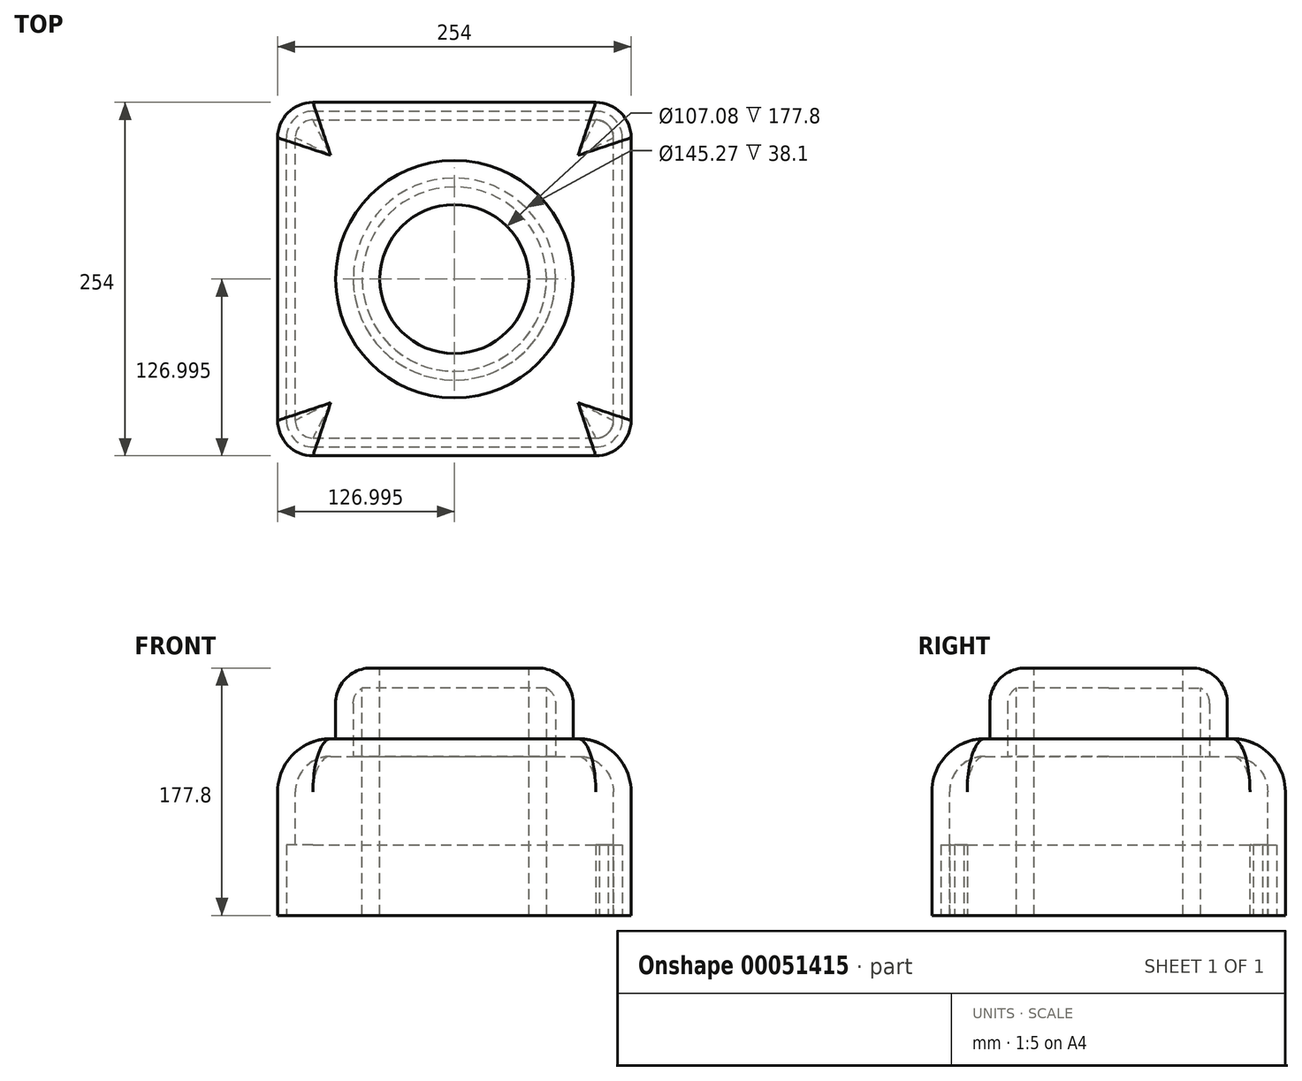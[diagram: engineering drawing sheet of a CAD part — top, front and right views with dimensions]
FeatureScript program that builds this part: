
annotation { "Feature Type Name" : "Feature", "Feature Type Description" : "" }
export const myFeature = defineFeature(function(context is Context, id is Id, definition is map)
    precondition{}
    {
        {
            var Q0;
            Q0=qCreatedBy(makeId("Top.planeOp"),FACE);
            var sketch = newSketch(context, id + "F0", { "sketchPlane" : qUnion([Q0])});
            skLineSegment(sketch, "E0.bottom", {"start": v(-164.41, -127.92) * mm, "end": v(89.59, -127.92) * mm});
            skLineSegment(sketch, "E0.top", {"start": v(-164.41, 126.08) * mm, "end": v(89.59, 126.08) * mm});
            skLineSegment(sketch, "E0.left", {"start": v(-164.41, -127.92) * mm, "end": v(-164.41, 126.08) * mm});
            skLineSegment(sketch, "E0.right", {"start": v(89.59, -127.92) * mm, "end": v(89.59, 126.08) * mm});
            skSolve(sketch);
        }
        {
            var Q0;
            Q0 = qSketchRegion(id + "F0", true);
            extrude(context, id + "F1", {"entities" : qUnion([Q0]), "depth" : 127 * mm});
        }
        {
            var Q0;
            Q0=makeQuery(id+"F1.opExtrude","CAP_FACE",FACE,{"disambiguationData":[OSD([sQuery(id+"F0.wireOp",EDGE,"E0.bottom"),sQuery(id+"F0.wireOp",EDGE,"E0.top"),sQuery(id+"F0.wireOp",EDGE,"E0.left"),sQuery(id+"F0.wireOp",EDGE,"E0.right")])],"isStart":false});
            var sketch = newSketch(context, id + "F2", { "sketchPlane" : qUnion([Q0])});
            skLineSegment(sketch, "E1", {"start": v(-164.41, 126.08) * mm, "end": v(-164.41, -127.92) * mm});
            skPoint(sketch, "E2.second.point", {"position": v(89.59, -127.92) * mm});
            skPoint(sketch, "E2.third.point", {"position": v(89.59, 126.08) * mm});
            skCircle(sketch, "E3", {"center": v(-37.41, -0.92) * mm, "radius": 85.34 * mm});
            skSolve(sketch);
        }
        {
            var Q0;
            Q0 = qSketchRegion(id + "F2", true);
            extrude(context, id + "F3", {"entities" : qUnion([Q0]), "operationType" : NewBodyOperationType.ADD, "depth" : 50.8 * mm});
        }
        {
            var Q0;
            Q0=makeQuery(id+"F3.opExtrude","CAP_FACE",FACE,{"disambiguationData":[OSD([sQuery(id+"F2.wireOp",EDGE,"E3")])],"isStart":false});
            var sketch = newSketch(context, id + "F4", { "sketchPlane" : qUnion([Q0])});
            skCircle(sketch, "E4", {"center": v(-37.41, -0.92) * mm, "radius": 53.54 * mm});
            skSolve(sketch);
        }
        {
            var Q0;
            Q0=makeQuery(id+"F4.imprint","IMPRINT",FACE,{"disambiguationData":[TD([[makeQuery(id+"F4.imprint","IMPRINT",EDGE,{"derivedFrom":sQuery(id+"F4.wireOp",EDGE,"E4")}),1.0]])]});
            var Q1;
            Q1=sQuery(id+"F4.wireOp",EDGE,"E4");
            var Q2;
            Q2=makeQuery(id+"F1.opExtrude","CAP_FACE",FACE,{"disambiguationData":[OSD([sQuery(id+"F0.wireOp",EDGE,"E0.bottom"),sQuery(id+"F0.wireOp",EDGE,"E0.top"),sQuery(id+"F0.wireOp",EDGE,"E0.left"),sQuery(id+"F0.wireOp",EDGE,"E0.right")])],"isStart":true});
            extrude(context, id + "F5", {"entities" : qUnion([Q0]), "operationType" : NewBodyOperationType.REMOVE, "surfaceEntities" : qUnion([Q1]), "endBound" : BoundingType.UP_TO_SURFACE, "oppositeDirection" : true, "endBoundEntityFace" : qUnion([Q2]), "depth" : 25.4 * mm});
        }
        {
            var Q0;
            Q0=makeQuery(id+"F1.opExtrude","SWEPT_EDGE",EDGE,{"disambiguationData":[OSD([sQuery(id+"F0.wireOp",EDGE,"E0.bottom"),sQuery(id+"F0.wireOp",EDGE,"E0.left")])]});
            var Q1;
            Q1=makeQuery(id+"F1.opExtrude","SWEPT_EDGE",EDGE,{"disambiguationData":[OSD([sQuery(id+"F0.wireOp",EDGE,"E0.bottom"),sQuery(id+"F0.wireOp",EDGE,"E0.right")])]});
            var Q2;
            Q2=makeQuery(id+"F1.opExtrude","SWEPT_EDGE",EDGE,{"disambiguationData":[OSD([sQuery(id+"F0.wireOp",EDGE,"E0.top"),sQuery(id+"F0.wireOp",EDGE,"E0.left")])]});
            var Q3;
            Q3=makeQuery(id+"F1.opExtrude","SWEPT_EDGE",EDGE,{"disambiguationData":[OSD([sQuery(id+"F0.wireOp",EDGE,"E0.top"),sQuery(id+"F0.wireOp",EDGE,"E0.right")])]});
            fillet(context, id + "F6", {"entities" : qUnion([Q0, Q1, Q2, Q3]), "radius" : 25.4 * mm, "tangentPropagation" : true, "allowEdgeOverflow" : false});
        }
        {
            var Q0;
            Q0=makeQuery(id+"F1.opExtrude","CAP_EDGE",EDGE,{"disambiguationData":[OSD([sQuery(id+"F0.wireOp",EDGE,"E0.top")])],"isStart":false});
            var Q1;
            Q1=makeQuery(id+"F1.opExtrude","CAP_EDGE",EDGE,{"disambiguationData":[OSD([sQuery(id+"F0.wireOp",EDGE,"E0.right")])],"isStart":false});
            var Q2;
            Q2=makeQuery(id+"F1.opExtrude","CAP_EDGE",EDGE,{"disambiguationData":[OSD([sQuery(id+"F0.wireOp",EDGE,"E0.left")])],"isStart":false});
            var Q3;
            Q3=makeQuery(id+"F1.opExtrude","CAP_EDGE",EDGE,{"disambiguationData":[OSD([sQuery(id+"F0.wireOp",EDGE,"E0.bottom")])],"isStart":false});
            fillet(context, id + "F7", {"entities" : qUnion([Q0, Q1, Q2, Q3]), "radius" : 38.1 * mm, "tangentPropagation" : true, "allowEdgeOverflow" : false});
        }
        {
            var Q0;
            Q0=makeQuery(id+"F3.opExtrude","CAP_EDGE",EDGE,{"disambiguationData":[OSD([sQuery(id+"F2.wireOp",EDGE,"E3")])],"isStart":false});
            fillet(context, id + "F8", {"entities" : qUnion([Q0]), "radius" : 25.4 * mm, "tangentPropagation" : true, "allowEdgeOverflow" : false});
        }
        {
            var Q0;
            Q0=makeQuery(id+"F1.opExtrude","CAP_FACE",FACE,{"disambiguationData":[OSD([sQuery(id+"F0.wireOp",EDGE,"E0.bottom"),sQuery(id+"F0.wireOp",EDGE,"E0.top"),sQuery(id+"F0.wireOp",EDGE,"E0.left"),sQuery(id+"F0.wireOp",EDGE,"E0.right")])],"isStart":true});
            shell(context, id + "F9", {"entities" : qUnion([Q0]), "thickness" : 12.7 * mm});
        }
        {
            var Q0;
            Q0=makeQuery(id+"F1.opExtrude","CAP_FACE",FACE,{"disambiguationData":[OSD([sQuery(id+"F0.wireOp",EDGE,"E0.bottom"),sQuery(id+"F0.wireOp",EDGE,"E0.top"),sQuery(id+"F0.wireOp",EDGE,"E0.left"),sQuery(id+"F0.wireOp",EDGE,"E0.right")])],"isStart":true});
            var sketch = newSketch(context, id + "F10", { "sketchPlane" : qUnion([Q0])});
            skArc(sketch, "E5.0", {"start": v(-139.01, 121.57) * mm, "mid": v(-152.49, 116) * mm, "end": v(-158.06, 102.52) * mm});
            skLineSegment(sketch, "E5.1", {"start": v(-139.01, 121.57) * mm, "end": v(64.19, 121.57) * mm});
            skLineSegment(sketch, "E5.2", {"start": v(-158.06, 102.52) * mm, "end": v(-158.06, -100.68) * mm});
            skArc(sketch, "E5.3", {"start": v(83.24, 102.52) * mm, "mid": v(77.66, 116) * mm, "end": v(64.19, 121.57) * mm});
            skArc(sketch, "E5.4", {"start": v(-158.06, -100.68) * mm, "mid": v(-152.49, -114.15) * mm, "end": v(-139.01, -119.73) * mm});
            skLineSegment(sketch, "E5.5", {"start": v(-139.01, -119.73) * mm, "end": v(64.19, -119.73) * mm});
            skArc(sketch, "E5.6", {"start": v(64.19, -119.73) * mm, "mid": v(77.66, -114.15) * mm, "end": v(83.24, -100.68) * mm});
            skLineSegment(sketch, "E5.7", {"start": v(83.24, 102.52) * mm, "end": v(83.24, -100.68) * mm});
            skLineSegment(sketch, "E6.0", {"start": v(-151.71, 102.52) * mm, "end": v(-151.71, -100.68) * mm});
            skArc(sketch, "E7.0", {"start": v(-139.01, 115.22) * mm, "mid": v(-148, 111.5) * mm, "end": v(-151.71, 102.52) * mm});
            skLineSegment(sketch, "E8.0", {"start": v(-139.01, 115.22) * mm, "end": v(64.19, 115.22) * mm});
            skFitSpline(sketch, "E9", {"points": [v(64.19, 115.22) * mm, v(65.02, 115.22) * mm, v(65.84, 115.14) * mm, v(66.66, 114.98) * mm, v(67.48, 114.82) * mm, v(68.27, 114.58) * mm, v(69.05, 114.26) * mm, v(69.82, 113.94) * mm, v(70.55, 113.55) * mm, v(71.24, 113.08) * mm, v(71.93, 112.62) * mm, v(72.58, 112.1) * mm, v(73.17, 111.5) * mm, v(73.75, 110.92) * mm, v(74.28, 110.27) * mm, v(74.74, 109.58) * mm, v(75.2, 108.89) * mm, v(75.6, 108.16) * mm, v(75.92, 107.39) * mm, v(76.24, 106.61) * mm, v(76.48, 105.82) * mm, v(76.64, 105) * mm, v(76.8, 104.18) * mm, v(76.89, 103.36) * mm, v(76.89, 102.52) * mm]});
            skLineSegment(sketch, "E10.0", {"start": v(76.89, 102.52) * mm, "end": v(76.89, -100.68) * mm});
            skFitSpline(sketch, "E11", {"points": [v(76.89, -100.68) * mm, v(76.89, -101.5) * mm, v(76.8, -102.33) * mm, v(76.64, -103.15) * mm, v(76.48, -103.97) * mm, v(76.24, -104.76) * mm, v(75.92, -105.54) * mm, v(75.6, -106.3) * mm, v(75.2, -107.04) * mm, v(74.74, -107.73) * mm, v(74.28, -108.42) * mm, v(73.76, -109.07) * mm, v(73.17, -109.66) * mm, v(72.58, -110.24) * mm, v(71.93, -110.77) * mm, v(71.24, -111.23) * mm, v(70.55, -111.7) * mm, v(69.82, -112.09) * mm, v(69.05, -112.4) * mm, v(68.28, -112.73) * mm, v(67.48, -112.97) * mm, v(66.66, -113.13) * mm, v(65.85, -113.3) * mm, v(65.02, -113.38) * mm, v(64.19, -113.38) * mm]});
            skLineSegment(sketch, "E12.0", {"start": v(-139.01, -113.38) * mm, "end": v(64.19, -113.38) * mm});
            skArc(sketch, "E13.0", {"start": v(-151.71, -100.68) * mm, "mid": v(-148, -109.66) * mm, "end": v(-139.01, -113.38) * mm});
            skSolve(sketch);
        }
        {
            var Q0;
            Q0=makeQuery(id+"F10.imprint","IMPRINT",FACE,{"disambiguationData":[TD([[makeQuery(id+"F10.imprint","IMPRINT",EDGE,{"derivedFrom":sQuery(id+"F10.wireOp",EDGE,"E5.0")}),1.0]])]});
            var Q1;
            Q1=sQuery(id+"F10.wireOp",EDGE,"E6.0");
            var Q2;
            Q2=sQuery(id+"F10.wireOp",EDGE,"E5.2");
            var Q3;
            Q3=sQuery(id+"F10.wireOp",EDGE,"E5.0");
            var Q4;
            Q4=sQuery(id+"F10.wireOp",EDGE,"E7.0");
            var Q5;
            Q5=sQuery(id+"F10.wireOp",EDGE,"E5.1");
            var Q6;
            Q6=sQuery(id+"F10.wireOp",EDGE,"E8.0");
            var Q7;
            Q7=sQuery(id+"F10.wireOp",EDGE,"E5.3");
            var Q8;
            Q8=sQuery(id+"F10.wireOp",EDGE,"E9");
            var Q9;
            Q9=sQuery(id+"F10.wireOp",EDGE,"E5.7");
            var Q10;
            Q10=sQuery(id+"F10.wireOp",EDGE,"E10.0");
            var Q11;
            Q11=sQuery(id+"F10.wireOp",EDGE,"E11");
            var Q12;
            Q12=sQuery(id+"F10.wireOp",EDGE,"E5.6");
            var Q13;
            Q13=sQuery(id+"F10.wireOp",EDGE,"E12.0");
            var Q14;
            Q14=sQuery(id+"F10.wireOp",EDGE,"E5.5");
            var Q15;
            Q15=sQuery(id+"F10.wireOp",EDGE,"E13.0");
            var Q16;
            Q16=sQuery(id+"F10.wireOp",EDGE,"E5.4");
            extrude(context, id + "F11", {"entities" : qUnion([Q0]), "operationType" : NewBodyOperationType.REMOVE, "surfaceEntities" : qUnion([Q1, Q2, Q3, Q4, Q5, Q6, Q7, Q8, Q9, Q10, Q11, Q12, Q13, Q14, Q15, Q16]), "oppositeDirection" : true, "depth" : 50.8 * mm});
        }
    });
